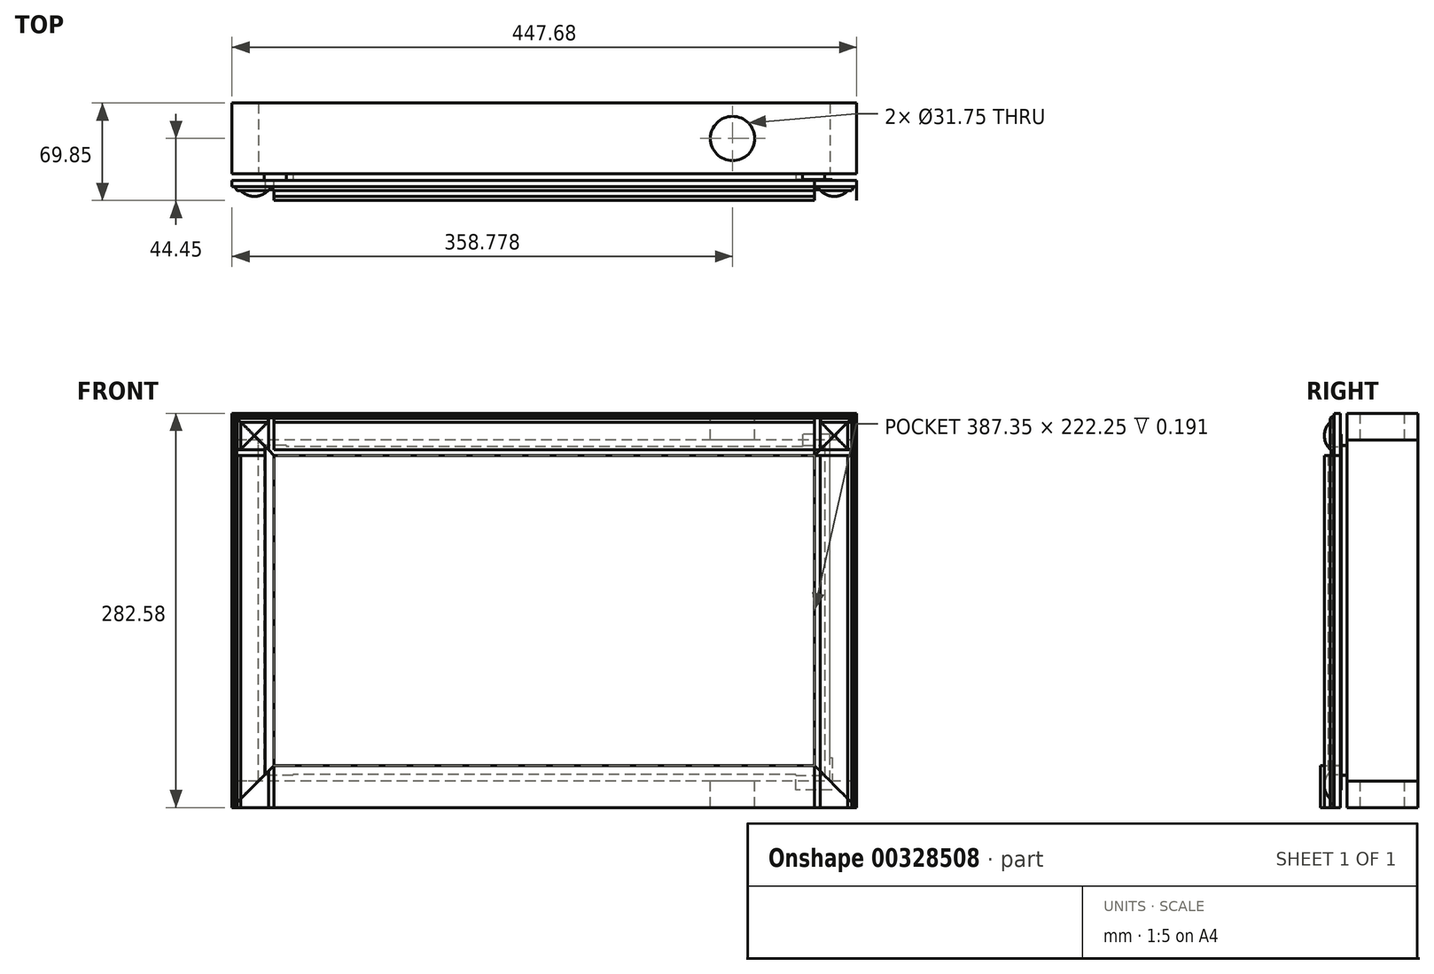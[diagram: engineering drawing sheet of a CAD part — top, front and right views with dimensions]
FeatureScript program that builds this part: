
annotation { "Feature Type Name" : "Feature", "Feature Type Description" : "" }
export const myFeature = defineFeature(function(context is Context, id is Id, definition is map)
    precondition{}
    {
        {
            var Q0;
            Q0=qCreatedBy(makeId("Front.planeOp"),FACE);
            var sketch = newSketch(context, id + "F0", { "sketchPlane" : qUnion([Q0])});
            skLineSegment(sketch, "E0.bottom", {"start": v(200.03, 117.48) * mm, "end": v(-200.03, 117.48) * mm});
            skLineSegment(sketch, "E0.top", {"start": v(200.03, -117.48) * mm, "end": v(-200.03, -117.48) * mm});
            skLineSegment(sketch, "E0.left", {"start": v(200.03, 117.48) * mm, "end": v(200.03, -117.47) * mm});
            skLineSegment(sketch, "E0.right", {"start": v(-200.03, 117.48) * mm, "end": v(-200.03, -117.48) * mm});
            skPoint(sketch, "E0.middle", {"position": v(0, 0) * mm});
            skLineSegment(sketch, "E1.bottom", {"start": v(-193.67, 111.13) * mm, "end": v(193.68, 111.13) * mm});
            skLineSegment(sketch, "E1.top", {"start": v(-193.68, -111.13) * mm, "end": v(193.67, -111.13) * mm});
            skLineSegment(sketch, "E1.left", {"start": v(-193.67, 111.13) * mm, "end": v(-193.68, -111.13) * mm});
            skLineSegment(sketch, "E1.right", {"start": v(193.68, 111.13) * mm, "end": v(193.67, -111.13) * mm});
            skSolve(sketch);
        }
        {
            var Q0;
            Q0=makeQuery(id+"F0.imprint","IMPRINT",FACE,{"disambiguationData":[TD([[makeQuery(id+"F0.imprint","IMPRINT",EDGE,{"derivedFrom":sQuery(id+"F0.wireOp",EDGE,"E0.bottom")}),1.0]])]});
            extrude(context, id + "F1", {"entities" : qUnion([Q0]), "depth" : 4.76 * mm});
        }
        {
            var Q0;
            Q0=makeQuery(id+"F0.imprint","IMPRINT",FACE,{"disambiguationData":[TD([[makeQuery(id+"F0.imprint","IMPRINT",EDGE,{"derivedFrom":sQuery(id+"F0.wireOp",EDGE,"E1.bottom")}),-1.0]])]});
            extrude(context, id + "F2", {"entities" : qUnion([Q0]), "operationType" : NewBodyOperationType.ADD, "depth" : 4.57 * mm});
        }
        {
            var Q0;
            Q0=makeQuery(id+"F1.opExtrude","CAP_FACE",FACE,{"disambiguationData":[OSD([sQuery(id+"F0.wireOp",EDGE,"E0.bottom"),sQuery(id+"F0.wireOp",EDGE,"E0.top"),sQuery(id+"F0.wireOp",EDGE,"E0.left"),sQuery(id+"F0.wireOp",EDGE,"E0.right"),sQuery(id+"F0.wireOp",EDGE,"E1.bottom"),sQuery(id+"F0.wireOp",EDGE,"E1.top"),sQuery(id+"F0.wireOp",EDGE,"E1.left"),sQuery(id+"F0.wireOp",EDGE,"E1.right")])],"isStart":false});
            var sketch = newSketch(context, id + "F3", { "sketchPlane" : qUnion([Q0])});
            skLineSegment(sketch, "E2.0", {"start": v(200.03, 117.48) * mm, "end": v(-200.03, 117.48) * mm});
            skLineSegment(sketch, "E3.0", {"start": v(-200.03, 117.48) * mm, "end": v(-200.03, -117.48) * mm});
            skLineSegment(sketch, "E4.0", {"start": v(200.03, -117.48) * mm, "end": v(-200.03, -117.48) * mm});
            skLineSegment(sketch, "E5.0", {"start": v(200.03, 117.48) * mm, "end": v(200.03, -117.47) * mm});
            skLineSegment(sketch, "E6", {"start": v(206.38, -117.48) * mm, "end": v(206.38, -105.57) * mm});
            skPoint(sketch, "E7", {"position": v(200.03, -105.57) * mm});
            skLineSegment(sketch, "E8", {"start": v(204.79, -105.57) * mm, "end": v(204.79, 117.48) * mm});
            skLineSegment(sketch, "E9", {"start": v(204.79, -105.57) * mm, "end": v(206.38, -105.57) * mm});
            skLineSegment(sketch, "E10", {"start": v(206.38, -117.48) * mm, "end": v(206.38, -128.59) * mm});
            skLineSegment(sketch, "E11", {"start": v(200.03, -128.59) * mm, "end": v(206.38, -128.59) * mm});
            skLineSegment(sketch, "E12", {"start": v(206.38, -128.59) * mm, "end": v(180.18, -128.59) * mm});
            skPoint(sketch, "E12.endSnap0", {"position": v(203.2, -128.59) * mm});
            skLineSegment(sketch, "E13", {"start": v(180.18, -128.59) * mm, "end": v(180.18, -117.48) * mm});
            skLineSegment(sketch, "E14", {"start": v(204.79, 117.48) * mm, "end": v(204.79, 126.2) * mm});
            skLineSegment(sketch, "E15", {"start": v(204.79, 126.2) * mm, "end": v(184.94, 126.2) * mm});
            skLineSegment(sketch, "E16", {"start": v(184.94, 126.2) * mm, "end": v(184.94, 117.48) * mm});
            skLineSegment(sketch, "E17.MirrorCS", {"start": v(-184.94, 126.2) * mm, "end": v(-184.94, 117.48) * mm});
            skLineSegment(sketch, "E18.MirrorCS", {"start": v(-204.79, 126.2) * mm, "end": v(-184.94, 126.2) * mm});
            skLineSegment(sketch, "E19.MirrorCS", {"start": v(-204.79, -105.57) * mm, "end": v(-204.79, 117.48) * mm});
            skLineSegment(sketch, "E20.MirrorCS", {"start": v(-204.79, 117.48) * mm, "end": v(-204.79, 126.2) * mm});
            skLineSegment(sketch, "E21.MirrorCS", {"start": v(-204.79, -105.57) * mm, "end": v(-206.38, -105.57) * mm});
            skLineSegment(sketch, "E22.MirrorCS", {"start": v(-206.38, -117.48) * mm, "end": v(-206.38, -105.57) * mm});
            skLineSegment(sketch, "E23.MirrorCS", {"start": v(-206.38, -117.48) * mm, "end": v(-206.38, -128.59) * mm});
            skLineSegment(sketch, "E24.MirrorCS", {"start": v(-206.38, -128.59) * mm, "end": v(-180.18, -128.59) * mm});
            skLineSegment(sketch, "E25.MirrorCS", {"start": v(-180.18, -128.59) * mm, "end": v(-180.18, -117.48) * mm});
            skLineSegment(sketch, "E26", {"start": v(-184.94, 117.48) * mm, "end": v(-184.94, 118.27) * mm});
            skLineSegment(sketch, "E27", {"start": v(-184.94, 118.27) * mm, "end": v(-200.82, 118.27) * mm});
            skLineSegment(sketch, "E28", {"start": v(-180.18, -117.48) * mm, "end": v(-180.18, -118.27) * mm});
            skLineSegment(sketch, "E29", {"start": v(-180.18, -118.27) * mm, "end": v(-200.82, -118.27) * mm});
            skLineSegment(sketch, "E30", {"start": v(-200.82, -117.48) * mm, "end": v(-200.82, -118.27) * mm});
            skLineSegment(sketch, "E31", {"start": v(-200.82, -117.48) * mm, "end": v(-200.82, 118.27) * mm});
            skLineSegment(sketch, "E32.MirrorCS", {"start": v(180.18, -118.27) * mm, "end": v(200.82, -118.27) * mm});
            skLineSegment(sketch, "E33.MirrorCS", {"start": v(200.82, -117.48) * mm, "end": v(200.82, -118.27) * mm});
            skLineSegment(sketch, "E34.MirrorCS", {"start": v(200.82, -117.48) * mm, "end": v(200.82, 118.27) * mm});
            skLineSegment(sketch, "E35.MirrorCS", {"start": v(184.94, 118.27) * mm, "end": v(200.82, 118.27) * mm});
            skSolve(sketch);
        }
        {
            var Q0;
            Q0=makeQuery(id+"F3.imprint","IMPRINT",FACE,{"disambiguationData":[TD([[makeQuery(id+"F3.imprint","IMPRINT",EDGE,{"derivedFrom":sQuery(id+"F3.wireOp",EDGE,"E17.MirrorCS")}),-1.0]])]});
            var Q1;
            {var subQ1=sQuery(id+"F3.wireOp",EDGE,"E3.0");Q1=makeQuery(id+"F3.imprint","IMPRINT",FACE,{"disambiguationData":[TD([[makeQuery(id+"F3.imprint","IMPRINT",EDGE,{"derivedFrom":subQ1}),-1.0]])]});}
            var Q2;
            Q2=makeQuery(id+"F3.imprint","IMPRINT",FACE,{"disambiguationData":[TD([[makeQuery(id+"F3.imprint","IMPRINT",EDGE,{"derivedFrom":sQuery(id+"F3.wireOp",EDGE,"E6")}),1.0]])]});
            var Q3;
            {var subQ0=sQuery(id+"F3.wireOp",EDGE,"E5.0");Q3=makeQuery(id+"F3.imprint","IMPRINT",FACE,{"disambiguationData":[TD([[makeQuery(id+"F3.imprint","IMPRINT",EDGE,{"derivedFrom":subQ0}),1.0]])]});}
            extrude(context, id + "F4", {"entities" : qUnion([Q0, Q1, Q2, Q3]), "oppositeDirection" : true, "depth" : 0.8 * mm});
        }
        {
            var Q0;
            {var subQ1=sQuery(id+"F3.wireOp",EDGE,"E3.0");Q0=makeQuery(id+"F3.imprint","IMPRINT",FACE,{"disambiguationData":[TD([[makeQuery(id+"F3.imprint","IMPRINT",EDGE,{"derivedFrom":subQ1}),-1.0]])]});}
            var Q1;
            {var subQ0=sQuery(id+"F3.wireOp",EDGE,"E5.0");Q1=makeQuery(id+"F3.imprint","IMPRINT",FACE,{"disambiguationData":[TD([[makeQuery(id+"F3.imprint","IMPRINT",EDGE,{"derivedFrom":subQ0}),1.0]])]});}
            extrude(context, id + "F5", {"entities" : qUnion([Q0, Q1]), "operationType" : NewBodyOperationType.ADD, "oppositeDirection" : true, "depth" : 4.76 * mm});
        }
        {
            var Q0;
            {var subQ2=sQuery(id+"F3.wireOp",EDGE,"E3.0");Q0=makeQuery(id+"F3.imprint","IMPRINT",FACE,{"disambiguationData":[TD([[makeQuery(id+"F3.imprint","IMPRINT",EDGE,{"derivedFrom":subQ2}),1.0]])]});}
            var sketch = newSketch(context, id + "F6", { "sketchPlane" : qUnion([Q0])});
            skLineSegment(sketch, "E36.0.0", {"start": v(180.18, -117.48) * mm, "end": v(200.03, -117.48) * mm});
            skLineSegment(sketch, "E36.0.1", {"start": v(200.03, -117.47) * mm, "end": v(200.03, 117.48) * mm});
            skLineSegment(sketch, "E36.0.2", {"start": v(200.03, 117.48) * mm, "end": v(184.94, 117.48) * mm});
            skLineSegment(sketch, "E36.0.3", {"start": v(184.94, 117.48) * mm, "end": v(-184.94, 117.48) * mm});
            skLineSegment(sketch, "E36.0.4", {"start": v(-184.94, 117.48) * mm, "end": v(-200.03, 117.48) * mm});
            skLineSegment(sketch, "E36.0.5", {"start": v(-200.03, 117.48) * mm, "end": v(-200.03, -117.48) * mm});
            skLineSegment(sketch, "E36.0.6", {"start": v(-200.03, -117.48) * mm, "end": v(-180.18, -117.48) * mm});
            skLineSegment(sketch, "E36.0.7", {"start": v(-180.18, -117.48) * mm, "end": v(180.18, -117.48) * mm});
            skLineSegment(sketch, "E37.0.0", {"start": v(-193.67, 111.13) * mm, "end": v(-193.68, -111.13) * mm});
            skLineSegment(sketch, "E37.0.1", {"start": v(-193.68, -111.13) * mm, "end": v(193.67, -111.13) * mm});
            skLineSegment(sketch, "E37.0.2", {"start": v(193.67, -111.13) * mm, "end": v(193.68, 111.13) * mm});
            skLineSegment(sketch, "E37.0.3", {"start": v(193.68, 111.13) * mm, "end": v(-193.67, 111.13) * mm});
            skLineSegment(sketch, "E38", {"start": v(193.68, 111.13) * mm, "end": v(193.68, 141.29) * mm, "construction": true});
            skLineSegment(sketch, "E39", {"start": v(193.68, 111.13) * mm, "end": v(223.84, 111.13) * mm, "construction": true});
            skLineSegment(sketch, "E40", {"start": v(193.67, -111.13) * mm, "end": v(223.84, -111.13) * mm, "construction": true});
            skLineSegment(sketch, "E41", {"start": v(193.67, -111.13) * mm, "end": v(193.67, -141.29) * mm, "construction": true});
            skLineSegment(sketch, "E42.MirrorCS", {"start": v(-193.68, 111.13) * mm, "end": v(-193.68, 141.29) * mm, "construction": true});
            skLineSegment(sketch, "E43.MirrorCS", {"start": v(-193.68, 111.13) * mm, "end": v(-223.84, 111.13) * mm, "construction": true});
            skLineSegment(sketch, "E44.MirrorCS", {"start": v(-193.67, -111.13) * mm, "end": v(-223.84, -111.13) * mm, "construction": true});
            skLineSegment(sketch, "E45.MirrorCS", {"start": v(-193.67, -111.13) * mm, "end": v(-193.67, -141.29) * mm, "construction": true});
            skLineSegment(sketch, "E46", {"start": v(-223.84, 111.13) * mm, "end": v(-223.84, -111.13) * mm});
            skLineSegment(sketch, "E47", {"start": v(-193.67, -141.29) * mm, "end": v(193.67, -141.29) * mm});
            skLineSegment(sketch, "E48", {"start": v(223.84, -111.13) * mm, "end": v(223.84, 111.13) * mm});
            skLineSegment(sketch, "E49", {"start": v(193.68, 141.29) * mm, "end": v(-193.68, 141.29) * mm});
            skLineSegment(sketch, "E50", {"start": v(-223.84, 111.13) * mm, "end": v(-223.84, 141.29) * mm});
            skLineSegment(sketch, "E51", {"start": v(223.84, 111.13) * mm, "end": v(223.84, 141.29) * mm});
            skLineSegment(sketch, "E52", {"start": v(-223.84, -111.13) * mm, "end": v(-223.84, -141.29) * mm});
            skLineSegment(sketch, "E53", {"start": v(-193.67, -141.29) * mm, "end": v(-223.84, -141.29) * mm});
            skLineSegment(sketch, "E54", {"start": v(193.67, -141.29) * mm, "end": v(223.84, -141.29) * mm});
            skLineSegment(sketch, "E55", {"start": v(193.68, 141.29) * mm, "end": v(223.84, 141.29) * mm});
            skLineSegment(sketch, "E56", {"start": v(-193.68, 141.29) * mm, "end": v(-223.84, 141.29) * mm});
            skLineSegment(sketch, "E57", {"start": v(223.84, -111.13) * mm, "end": v(223.84, -141.29) * mm});
            skLineSegment(sketch, "E58", {"start": v(193.68, 111.13) * mm, "end": v(200.03, 117.48) * mm});
            skLineSegment(sketch, "E59", {"start": v(193.67, -111.13) * mm, "end": v(200.03, -117.48) * mm});
            skLineSegment(sketch, "E60", {"start": v(-193.68, -111.13) * mm, "end": v(-200.03, -117.48) * mm});
            skLineSegment(sketch, "E61", {"start": v(-193.67, 111.13) * mm, "end": v(-200.02, 117.48) * mm});
            skLineSegment(sketch, "E62", {"start": v(-200.03, 117.48) * mm, "end": v(-193.67, 111.13) * mm});
            skLineSegment(sketch, "E63", {"start": v(-200.03, -117.48) * mm, "end": v(-193.68, -111.13) * mm});
            skLineSegment(sketch, "E64", {"start": v(-200.03, -117.48) * mm, "end": v(-200.03, 117.48) * mm});
            skLineSegment(sketch, "E65", {"start": v(193.68, 111.13) * mm, "end": v(193.67, -111.13) * mm});
            skLineSegment(sketch, "E66", {"start": v(200.03, -117.48) * mm, "end": v(200.03, 117.48) * mm});
            skLineSegment(sketch, "E67", {"start": v(200.03, 117.48) * mm, "end": v(-200.03, 117.48) * mm});
            skLineSegment(sketch, "E68", {"start": v(-200.03, -117.47) * mm, "end": v(200.03, -117.47) * mm});
            skLineSegment(sketch, "E69", {"start": v(193.67, -111.13) * mm, "end": v(-193.68, -111.13) * mm});
            skLineSegment(sketch, "E70", {"start": v(-200.02, 117.48) * mm, "end": v(-223.84, 141.29) * mm});
            skLineSegment(sketch, "E71", {"start": v(-200.03, -117.48) * mm, "end": v(-223.84, -141.29) * mm});
            skLineSegment(sketch, "E72", {"start": v(200.03, -117.48) * mm, "end": v(223.84, -141.29) * mm});
            skLineSegment(sketch, "E73", {"start": v(200.03, 117.48) * mm, "end": v(223.84, 141.29) * mm});
            skSolve(sketch);
        }
        {
            var Q0;
            Q0=makeQuery(id+"F6.imprint","IMPRINT",FACE,{"disambiguationData":[TD([[makeQuery(id+"F6.imprint","IMPRINT",EDGE,{"derivedFrom":sQuery(id+"F6.wireOp",EDGE,"E37.0.3")}),1.0]])]});
            var Q1;
            {var subQ3=sQuery(id+"F6.wireOp",EDGE,"E59");Q1=makeQuery(id+"F6.imprint","IMPRINT",FACE,{"disambiguationData":[TD([[makeQuery(id+"F6.imprint","IMPRINT",EDGE,{"derivedFrom":subQ3}),-1.0]])]});}
            var Q2;
            Q2=makeQuery(id+"F6.imprint","IMPRINT",FACE,{"disambiguationData":[TD([[makeQuery(id+"F6.imprint","IMPRINT",EDGE,{"derivedFrom":sQuery(id+"F6.wireOp",EDGE,"E47")}),1.0]])]});
            var Q3;
            Q3=makeQuery(id+"F6.imprint","IMPRINT",FACE,{"disambiguationData":[TD([[makeQuery(id+"F6.imprint","IMPRINT",EDGE,{"derivedFrom":sQuery(id+"F6.wireOp",EDGE,"E49")}),1.0]])]});
            extrude(context, id + "F7", {"entities" : qUnion([Q0, Q1, Q2, Q3]), "depth" : 14.29 * mm});
        }
        {
            var Q0;
            Q0=makeQuery(id+"F6.imprint","IMPRINT",FACE,{"disambiguationData":[TD([[makeQuery(id+"F6.imprint","IMPRINT",EDGE,{"derivedFrom":sQuery(id+"F6.wireOp",EDGE,"E46")}),1.0]])]});
            var Q1;
            Q1=makeQuery(id+"F6.imprint","IMPRINT",FACE,{"disambiguationData":[TD([[makeQuery(id+"F6.imprint","IMPRINT",EDGE,{"derivedFrom":sQuery(id+"F6.wireOp",EDGE,"E62")}),-1.0]])]});
            var Q2;
            Q2=makeQuery(id+"F6.imprint","IMPRINT",FACE,{"disambiguationData":[TD([[makeQuery(id+"F6.imprint","IMPRINT",EDGE,{"derivedFrom":sQuery(id+"F6.wireOp",EDGE,"E58")}),-1.0]])]});
            var Q3;
            Q3=makeQuery(id+"F6.imprint","IMPRINT",FACE,{"disambiguationData":[TD([[makeQuery(id+"F6.imprint","IMPRINT",EDGE,{"derivedFrom":sQuery(id+"F6.wireOp",EDGE,"E48")}),1.0]])]});
            extrude(context, id + "F8", {"entities" : qUnion([Q0, Q1, Q2, Q3]), "depth" : 14.29 * mm});
        }
        {
            var Q0;
            Q0=makeQuery(id+"F8.opExtrude","SWEPT_FACE",FACE,{"disambiguationData":[OSD([sQuery(id+"F6.wireOp",EDGE,"E48"),sQuery(id+"F6.wireOp",EDGE,"E51"),sQuery(id+"F6.wireOp",EDGE,"E57")])]});
            var sketch = newSketch(context, id + "F9", { "sketchPlane" : qUnion([Q0])});
            skPoint(sketch, "E74.0", {"position": v(-4.76, 111.12) * mm});
            skPoint(sketch, "E75.0", {"position": v(-19.05, 111.12) * mm});
            skLineSegment(sketch, "E76", {"start": v(-19.05, 111.12) * mm, "end": v(-4.76, 111.12) * mm});
            skLineSegment(sketch, "E77", {"start": v(-19.05, 111.12) * mm, "end": v(-19.05, 141.29) * mm});
            skLineSegment(sketch, "E78", {"start": v(-4.76, 111.12) * mm, "end": v(-4.76, 141.29) * mm});
            skLineSegment(sketch, "E79", {"start": v(-4.76, 141.29) * mm, "end": v(-19.05, 141.29) * mm});
            skLineSegment(sketch, "E80.0.2", {"start": v(-19.05, 141.29) * mm, "end": v(-19.05, 111.12) * mm});
            skPoint(sketch, "E81", {"position": v(-4.76, 141.29) * mm});
            skPoint(sketch, "E82", {"position": v(-19.05, 141.29) * mm});
            skPoint(sketch, "E83", {"position": v(-11.35, 111.13) * mm});
            skPoint(sketch, "E84", {"position": v(-8.95, 141.29) * mm});
            skPoint(sketch, "E85", {"position": v(-11.84, 134.98) * mm});
            skPoint(sketch, "E86", {"position": v(-11.34, 115.03) * mm});
            skPoint(sketch, "E87", {"position": v(-11.8, 137.67) * mm});
            skPoint(sketch, "E88", {"position": v(-9.2, 139.35) * mm});
            skLineSegment(sketch, "E89", {"start": v(-8.95, 141.29) * mm, "end": v(-9.2, 139.35) * mm});
            skLineSegment(sketch, "E90", {"start": v(-11.8, 137.67) * mm, "end": v(-9.2, 139.35) * mm});
            skLineSegment(sketch, "E91", {"start": v(-11.8, 137.67) * mm, "end": v(-11.84, 134.98) * mm});
            skLineSegment(sketch, "E92", {"start": v(-11.35, 111.13) * mm, "end": v(-11.34, 115.03) * mm});
            skArc(sketch, "E93", {"start": v(-11.84, 134.98) * mm, "mid": v(-16.1, 124.9) * mm, "end": v(-11.34, 115.03) * mm});
            skLineSegment(sketch, "E94", {"start": v(-4.74, 111.13) * mm, "end": v(-11.35, 111.13) * mm});
            skLineSegment(sketch, "E95", {"start": v(-4.74, 111.13) * mm, "end": v(-4.74, 141.29) * mm});
            skLineSegment(sketch, "E96", {"start": v(-4.74, 141.29) * mm, "end": v(-8.95, 141.29) * mm});
            skLineSegment(sketch, "E97.MirrorCS", {"start": v(-19.05, -111.13) * mm, "end": v(-19.05, -141.29) * mm});
            skPoint(sketch, "E98.MirrorP", {"position": v(-4.76, 171.45) * mm});
            skLineSegment(sketch, "E99.MirrorCS", {"start": v(-19.05, -111.13) * mm, "end": v(-4.76, -111.13) * mm});
            skPoint(sketch, "E100.MirrorP", {"position": v(-19.05, 171.45) * mm});
            skArc(sketch, "E101.MirrorCS", {"start": v(-11.84, -134.98) * mm, "mid": v(-16.1, -124.9) * mm, "end": v(-11.34, -115.03) * mm});
            skPoint(sketch, "E102.MirrorP", {"position": v(-11.84, 147.6) * mm});
            skPoint(sketch, "E103.MirrorP", {"position": v(-11.35, 171.44) * mm});
            skPoint(sketch, "E104.MirrorP", {"position": v(-11.8, 144.9) * mm});
            skLineSegment(sketch, "E105.MirrorCS", {"start": v(-11.35, -111.13) * mm, "end": v(-11.34, -115.03) * mm});
            skLineSegment(sketch, "E106.MirrorCS", {"start": v(-11.8, -137.67) * mm, "end": v(-9.2, -139.35) * mm});
            skLineSegment(sketch, "E107.MirrorCS", {"start": v(-8.95, -141.29) * mm, "end": v(-9.2, -139.35) * mm});
            skLineSegment(sketch, "E108.MirrorCS", {"start": v(-4.76, -111.13) * mm, "end": v(-4.76, -141.29) * mm});
            skLineSegment(sketch, "E109.MirrorCS", {"start": v(-11.8, -137.67) * mm, "end": v(-11.84, -134.98) * mm});
            skPoint(sketch, "E110.MirrorP", {"position": v(-9.2, 143.23) * mm});
            skPoint(sketch, "E111.MirrorP", {"position": v(-11.34, 167.54) * mm});
            skLineSegment(sketch, "E112", {"start": v(-19.05, -141.29) * mm, "end": v(-8.95, -141.29) * mm});
            skLineSegment(sketch, "E113", {"start": v(-8.95, -141.29) * mm, "end": v(-4.76, -141.29) * mm});
            skLineSegment(sketch, "E114", {"start": v(-11.35, -111.13) * mm, "end": v(-11.35, -111.13) * mm});
            skSolve(sketch);
        }
        {
            var Q0;
            {var subQ1=sQuery(id+"F9.wireOp",EDGE,"E97.MirrorCS");Q0=makeQuery(id+"F9.imprint","IMPRINT",FACE,{"disambiguationData":[TD([[makeQuery(id+"F9.imprint","IMPRINT",EDGE,{"derivedFrom":subQ1}),1.0]])]});}
            var Q1;
            {var subQ2=sQuery(id+"F9.wireOp",EDGE,"E76");Q1=makeQuery(id+"F9.imprint","IMPRINT",FACE,{"disambiguationData":[TD([[makeQuery(id+"F9.imprint","IMPRINT",EDGE,{"derivedFrom":subQ2}),1.0]])]});}
            extrude(context, id + "F10", {"entities" : qUnion([Q0, Q1]), "operationType" : NewBodyOperationType.REMOVE, "oppositeDirection" : true, "depth" : 508 * mm});
        }
        {
            var Q0;
            Q0=qCreatedBy(makeId("Front.planeOp"),FACE);
            var sketch = newSketch(context, id + "F11", { "sketchPlane" : qUnion([Q0])});
            skLineSegment(sketch, "E115.0.1", {"start": v(-200.03, 117.48) * mm, "end": v(-184.94, 117.48) * mm});
            skLineSegment(sketch, "E115.0.2", {"start": v(-184.94, 117.48) * mm, "end": v(184.94, 117.48) * mm});
            skLineSegment(sketch, "E115.0.3", {"start": v(184.94, 117.48) * mm, "end": v(200.03, 117.48) * mm});
            skLineSegment(sketch, "E115.0.5", {"start": v(223.84, 141.29) * mm, "end": v(193.68, 141.29) * mm});
            skLineSegment(sketch, "E115.0.6", {"start": v(193.68, 141.29) * mm, "end": v(-193.68, 141.29) * mm});
            skLineSegment(sketch, "E115.0.7", {"start": v(-193.68, 141.29) * mm, "end": v(-223.84, 141.29) * mm});
            skLineSegment(sketch, "E116.0.0", {"start": v(200.03, 117.48) * mm, "end": v(200.03, -117.47) * mm});
            skLineSegment(sketch, "E116.0.2", {"start": v(223.84, -141.29) * mm, "end": v(223.84, -111.13) * mm});
            skLineSegment(sketch, "E116.0.3", {"start": v(223.84, -111.13) * mm, "end": v(223.84, 111.13) * mm});
            skLineSegment(sketch, "E116.0.4", {"start": v(223.84, 111.13) * mm, "end": v(223.84, 141.29) * mm});
            skLineSegment(sketch, "E117.0.1", {"start": v(200.03, -117.48) * mm, "end": v(180.18, -117.48) * mm});
            skLineSegment(sketch, "E117.0.2", {"start": v(180.18, -117.48) * mm, "end": v(-180.18, -117.48) * mm});
            skLineSegment(sketch, "E117.0.3", {"start": v(-180.18, -117.48) * mm, "end": v(-200.03, -117.48) * mm});
            skLineSegment(sketch, "E117.0.5", {"start": v(-223.84, -141.29) * mm, "end": v(-193.67, -141.29) * mm});
            skLineSegment(sketch, "E117.0.6", {"start": v(-193.67, -141.29) * mm, "end": v(193.67, -141.29) * mm});
            skLineSegment(sketch, "E117.0.7", {"start": v(193.67, -141.29) * mm, "end": v(223.84, -141.29) * mm});
            skLineSegment(sketch, "E118.0.1", {"start": v(-200.03, -117.48) * mm, "end": v(-200.03, 117.48) * mm});
            skLineSegment(sketch, "E118.0.3", {"start": v(-223.84, 141.29) * mm, "end": v(-223.84, 111.13) * mm});
            skLineSegment(sketch, "E118.0.4", {"start": v(-223.84, 111.13) * mm, "end": v(-223.84, -111.13) * mm});
            skLineSegment(sketch, "E118.0.5", {"start": v(-223.84, -111.13) * mm, "end": v(-223.84, -141.29) * mm});
            skLineSegment(sketch, "E119", {"start": v(223.84, 141.29) * mm, "end": v(223.84, 122.24) * mm});
            skLineSegment(sketch, "E120", {"start": v(223.84, 122.24) * mm, "end": v(-223.84, 122.24) * mm});
            skLineSegment(sketch, "E121", {"start": v(223.84, -141.29) * mm, "end": v(223.84, -122.24) * mm});
            skLineSegment(sketch, "E122", {"start": v(223.84, -122.24) * mm, "end": v(-223.84, -122.24) * mm});
            skLineSegment(sketch, "E123", {"start": v(-223.84, 122.24) * mm, "end": v(-204.79, 122.24) * mm});
            skLineSegment(sketch, "E124", {"start": v(-223.84, -122.24) * mm, "end": v(-204.79, -122.24) * mm});
            skLineSegment(sketch, "E125", {"start": v(-204.79, -122.24) * mm, "end": v(-204.79, 122.24) * mm});
            skLineSegment(sketch, "E126", {"start": v(223.84, 122.24) * mm, "end": v(204.79, 122.24) * mm});
            skLineSegment(sketch, "E127", {"start": v(223.84, -122.24) * mm, "end": v(204.79, -122.24) * mm});
            skLineSegment(sketch, "E128", {"start": v(204.79, -122.24) * mm, "end": v(204.79, 122.24) * mm});
            skSolve(sketch);
        }
        {
            var Q0;
            Q0=makeQuery(id+"F11.imprint","IMPRINT",FACE,{"disambiguationData":[TD([[makeQuery(id+"F11.imprint","IMPRINT",EDGE,{"derivedFrom":sQuery(id+"F11.wireOp",EDGE,"E115.0.5")}),1.0]])]});
            var Q1;
            {var subQ1=sQuery(id+"F11.wireOp",EDGE,"E117.0.5");Q1=makeQuery(id+"F11.imprint","IMPRINT",FACE,{"disambiguationData":[TD([[makeQuery(id+"F11.imprint","IMPRINT",EDGE,{"derivedFrom":subQ1}),1.0]])]});}
            extrude(context, id + "F12", {"entities" : qUnion([Q0, Q1]), "oppositeDirection" : true, "depth" : 50.8 * mm});
        }
        {
            var Q0;
            Q0=makeQuery(id+"F11.imprint","IMPRINT",FACE,{"disambiguationData":[TD([[makeQuery(id+"F11.imprint","IMPRINT",EDGE,{"derivedFrom":sQuery(id+"F11.wireOp",EDGE,"E116.0.2")}),1.0]])]});
            var Q1;
            {var subQ2=sQuery(id+"F11.wireOp",EDGE,"E118.0.4");Q1=makeQuery(id+"F11.imprint","IMPRINT",FACE,{"disambiguationData":[TD([[makeQuery(id+"F11.imprint","IMPRINT",EDGE,{"derivedFrom":subQ2}),1.0]])]});}
            extrude(context, id + "F13", {"entities" : qUnion([Q0, Q1]), "oppositeDirection" : true, "depth" : 50.8 * mm});
        }
        {
            var Q0;
            Q0=makeQuery(id+"F12.opExtrude","SWEPT_FACE",FACE,{"disambiguationData":[OSD([sQuery(id+"F11.wireOp",EDGE,"E117.0.5"),sQuery(id+"F11.wireOp",EDGE,"E117.0.6"),sQuery(id+"F11.wireOp",EDGE,"E117.0.7")])]});
            var sketch = newSketch(context, id + "F14", { "sketchPlane" : qUnion([Q0])});
            skPoint(sketch, "E129.0", {"position": v(-223.84, 19.05) * mm});
            skPoint(sketch, "E130.0", {"position": v(-223.84, 4.76) * mm});
            skPoint(sketch, "E131.0", {"position": v(-193.68, 19.05) * mm});
            skPoint(sketch, "E132.0", {"position": v(223.84, 19.05) * mm});
            skPoint(sketch, "E133.0", {"position": v(223.84, 4.76) * mm});
            skPoint(sketch, "E134.0", {"position": v(193.67, 19.05) * mm});
            skPoint(sketch, "E135.0", {"position": v(193.67, 4.76) * mm});
            skPoint(sketch, "E136.0", {"position": v(-193.67, 4.76) * mm});
            skPoint(sketch, "E137.0", {"position": v(193.67, 4.78) * mm});
            skPoint(sketch, "E138.0", {"position": v(193.67, 19.07) * mm});
            skLineSegment(sketch, "E139", {"start": v(193.67, 19.07) * mm, "end": v(193.67, 4.78) * mm});
            skLineSegment(sketch, "E140", {"start": v(193.67, 19.07) * mm, "end": v(223.83, 19.07) * mm});
            skLineSegment(sketch, "E141", {"start": v(193.67, 4.78) * mm, "end": v(223.83, 4.78) * mm});
            skLineSegment(sketch, "E142", {"start": v(223.83, 4.78) * mm, "end": v(223.83, 19.07) * mm});
            skLineSegment(sketch, "E143.0.2", {"start": v(223.83, 19.07) * mm, "end": v(193.67, 19.07) * mm});
            skPoint(sketch, "E144", {"position": v(223.83, 4.78) * mm});
            skPoint(sketch, "E145", {"position": v(223.83, 19.07) * mm});
            skPoint(sketch, "E146", {"position": v(193.67, 11.37) * mm});
            skPoint(sketch, "E147", {"position": v(223.83, 8.97) * mm});
            skPoint(sketch, "E148", {"position": v(217.52, 11.86) * mm});
            skPoint(sketch, "E149", {"position": v(197.58, 11.37) * mm});
            skPoint(sketch, "E150", {"position": v(220.21, 11.83) * mm});
            skPoint(sketch, "E151", {"position": v(221.9, 9.22) * mm});
            skLineSegment(sketch, "E152", {"start": v(223.83, 8.97) * mm, "end": v(221.9, 9.22) * mm});
            skLineSegment(sketch, "E153", {"start": v(220.21, 11.83) * mm, "end": v(221.9, 9.22) * mm});
            skLineSegment(sketch, "E154", {"start": v(220.21, 11.83) * mm, "end": v(217.52, 11.86) * mm});
            skLineSegment(sketch, "E155", {"start": v(193.67, 11.37) * mm, "end": v(197.58, 11.37) * mm});
            skArc(sketch, "E156", {"start": v(217.52, 11.86) * mm, "mid": v(207.44, 16.12) * mm, "end": v(197.58, 11.37) * mm});
            skLineSegment(sketch, "E157", {"start": v(193.67, 4.76) * mm, "end": v(193.67, 11.37) * mm});
            skLineSegment(sketch, "E158", {"start": v(193.67, 4.76) * mm, "end": v(223.83, 4.76) * mm});
            skLineSegment(sketch, "E159", {"start": v(223.83, 4.76) * mm, "end": v(223.83, 8.97) * mm});
            skLineSegment(sketch, "E160.MirrorCS", {"start": v(-193.68, 19.05) * mm, "end": v(-223.84, 19.05) * mm});
            skPoint(sketch, "E161.MirrorP", {"position": v(114.44, -159.82) * mm});
            skLineSegment(sketch, "E162.MirrorCS", {"start": v(-193.68, 19.05) * mm, "end": v(-193.68, 4.76) * mm});
            skPoint(sketch, "E163.MirrorP", {"position": v(114.44, -145.53) * mm});
            skArc(sketch, "E164.MirrorCS", {"start": v(-217.53, 11.84) * mm, "mid": v(-207.45, 16.1) * mm, "end": v(-197.58, 11.34) * mm});
            skPoint(sketch, "E165.MirrorP", {"position": v(230.14, 11.86) * mm});
            skPoint(sketch, "E166.MirrorP", {"position": v(114.44, -153.24) * mm});
            skPoint(sketch, "E167.MirrorP", {"position": v(227.45, 11.83) * mm});
            skLineSegment(sketch, "E168.MirrorCS", {"start": v(-193.68, 11.35) * mm, "end": v(-197.58, 11.34) * mm});
            skLineSegment(sketch, "E169.MirrorCS", {"start": v(-220.22, 11.8) * mm, "end": v(-221.9, 9.2) * mm});
            skLineSegment(sketch, "E170.MirrorCS", {"start": v(-223.84, 8.95) * mm, "end": v(-221.9, 9.2) * mm});
            skLineSegment(sketch, "E171.MirrorCS", {"start": v(-193.68, 4.76) * mm, "end": v(-223.84, 4.76) * mm});
            skLineSegment(sketch, "E172.MirrorCS", {"start": v(-220.22, 11.8) * mm, "end": v(-217.53, 11.84) * mm});
            skPoint(sketch, "E173.MirrorP", {"position": v(225.77, 9.22) * mm});
            skPoint(sketch, "E174.MirrorP", {"position": v(110.53, -153.24) * mm});
            skLineSegment(sketch, "E175", {"start": v(-223.84, 19.05) * mm, "end": v(-223.84, 8.95) * mm});
            skLineSegment(sketch, "E176", {"start": v(-223.84, 8.95) * mm, "end": v(-223.84, 4.76) * mm});
            skLineSegment(sketch, "E177", {"start": v(-193.68, 11.35) * mm, "end": v(-193.68, 11.35) * mm});
            skSolve(sketch);
        }
        {
            var Q0;
            {var subQ2=sQuery(id+"F14.wireOp",EDGE,"E139");Q0=makeQuery(id+"F14.imprint","IMPRINT",FACE,{"disambiguationData":[TD([[makeQuery(id+"F14.imprint","IMPRINT",EDGE,{"derivedFrom":subQ2}),1.0]])]});}
            var Q1;
            {var subQ1=sQuery(id+"F14.wireOp",EDGE,"E160.MirrorCS");Q1=makeQuery(id+"F14.imprint","IMPRINT",FACE,{"disambiguationData":[TD([[makeQuery(id+"F14.imprint","IMPRINT",EDGE,{"derivedFrom":subQ1}),1.0]])]});}
            extrude(context, id + "F15", {"entities" : qUnion([Q0, Q1]), "operationType" : NewBodyOperationType.REMOVE, "oppositeDirection" : true, "depth" : 508 * mm});
        }
        {
            var Q0;
            Q0=makeQuery(id+"F12.opExtrude","SWEPT_FACE",FACE,{"disambiguationData":[OSD([sQuery(id+"F11.wireOp",EDGE,"E115.0.5"),sQuery(id+"F11.wireOp",EDGE,"E115.0.6"),sQuery(id+"F11.wireOp",EDGE,"E115.0.7")])]});
            var sketch = newSketch(context, id + "F16", { "sketchPlane" : qUnion([Q0])});
            skLineSegment(sketch, "E178", {"start": v(223.84, 25.4) * mm, "end": v(134.94, 25.4) * mm, "construction": true});
            skCircle(sketch, "E179", {"center": v(134.94, 25.4) * mm, "radius": 15.88 * mm});
            skSolve(sketch);
        }
        {
            var Q0;
            Q0=makeQuery(id+"F16.imprint","IMPRINT",FACE,{"disambiguationData":[TD([[makeQuery(id+"F16.imprint","IMPRINT",EDGE,{"derivedFrom":sQuery(id+"F16.wireOp",EDGE,"E179")}),1.0]])]});
            extrude(context, id + "F17", {"entities" : qUnion([Q0]), "operationType" : NewBodyOperationType.REMOVE, "oppositeDirection" : true, "depth" : 508 * mm});
        }
    });
